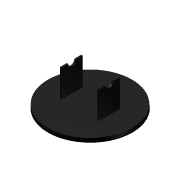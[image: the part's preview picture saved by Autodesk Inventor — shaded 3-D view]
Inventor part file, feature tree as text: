
AUTODESK INVENTOR PART (.ipt)
format: ipt  version: 2012 (Build 160160000, 160)  size: 104,960 bytes
history: native  units: mm
features: extrude x3, sketch x2
ambient origin geometry x8: Origin, YZ Plane, XZ Plane, XY Plane, X Axis, Y Axis, Z Axis, Center Point
bodies: Solid1 (feature_tree)
feature tree (5):
  sketch  "Sketch1"  dims[d0=4.7625mm d1=0.0mm d2=40.7625mm d3=0.0mm]
  extrude  "Extrusion1"  Depth=40.7625mm TaperAngle=0.0deg
  extrude  "Extrusion2"  [1 undecoded]
  extrude  "Extrusion3"  [1 undecoded]
  sketch  "Sketch2"  dims[d4=40.7625mm d5=0.0mm]
note: 2 required parameter values undecoded (feature->parameter linkage not recoverable at this tier; creation-order binding heuristic only, values carry confidence <= 0.55)
